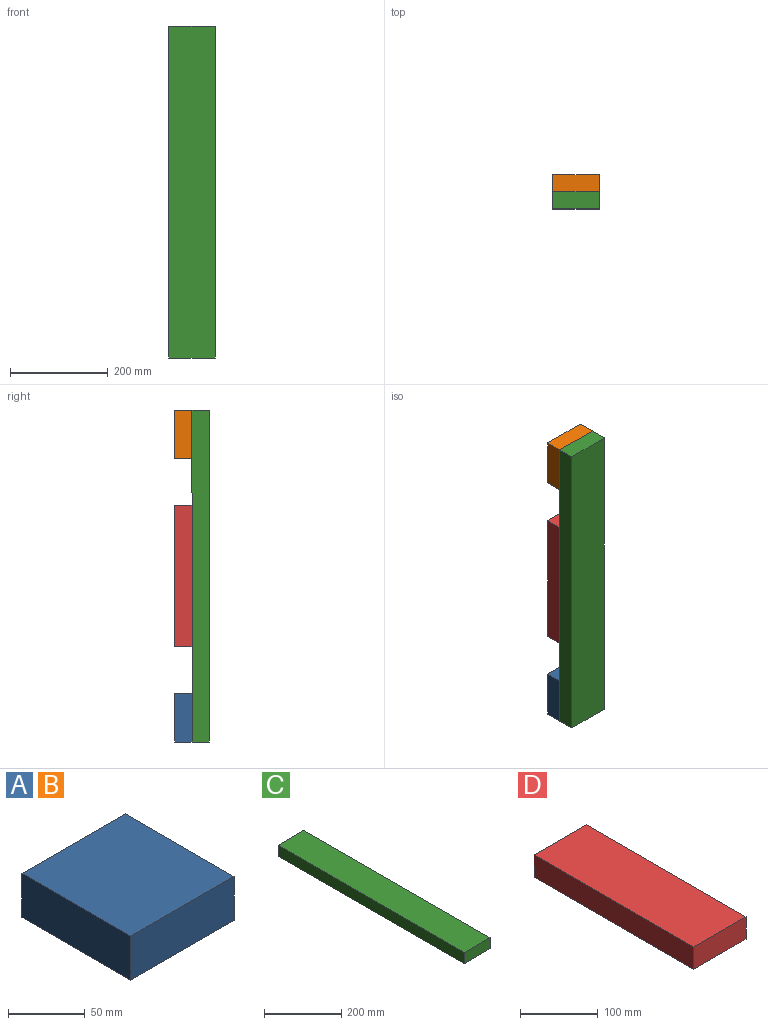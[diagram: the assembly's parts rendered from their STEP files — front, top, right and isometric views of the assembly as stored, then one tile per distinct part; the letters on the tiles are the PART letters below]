
ASSEMBLY  parts=4 mates=3
PART A: 6 faces, bbox 95x100x35 mm
  f0: plane 100x35mm, normal (1,0,0), area 3500mm2, adj f1,f3,f4,f5
  f1: plane 100x95mm, normal (0,0,1), area 9500mm2, adj f0,f2,f4,f5
  f2: plane 100x35mm, normal (-1,0,0), area 3500mm2, adj f1,f3,f4,f5
  f3: plane 100x95mm, normal (0,0,-1), area 9500mm2, adj f0,f2,f4,f5
  f4: plane 95x35mm, normal (0,-1,0), area 3325mm2, adj f0,f1,f2,f3
  f5: plane 95x35mm, normal (0,1,0), area 3325mm2, adj f0,f1,f2,f3
PART B: same geometry as A
PART C: 6 faces, bbox 95x680x35 mm
  f0: plane 680x35mm, normal (1,0,0), area 23800mm2, adj f1,f3,f4,f5
  f1: plane 680x95mm, normal (0,0,1), area 64600mm2, adj f0,f2,f4,f5
  f2: plane 680x35mm, normal (-1,0,0), area 23800mm2, adj f1,f3,f4,f5
  f3: plane 680x95mm, normal (0,0,-1), area 64600mm2, adj f0,f2,f4,f5
  f4: plane 95x35mm, normal (0,-1,0), area 3325mm2, adj f0,f1,f2,f3
  f5: plane 95x35mm, normal (0,1,0), area 3325mm2, adj f0,f1,f2,f3
PART D: 6 faces, bbox 95x290x35 mm
  f0: plane 290x35mm, normal (1,0,0), area 10150mm2, adj f1,f3,f4,f5
  f1: plane 290x95mm, normal (0,0,1), area 27550mm2, adj f0,f2,f4,f5
  f2: plane 290x35mm, normal (-1,0,0), area 10150mm2, adj f1,f3,f4,f5
  f3: plane 290x95mm, normal (0,0,-1), area 27550mm2, adj f0,f2,f4,f5
  f4: plane 95x35mm, normal (0,-1,0), area 3325mm2, adj f0,f1,f2,f3
  f5: plane 95x35mm, normal (0,1,0), area 3325mm2, adj f0,f1,f2,f3
PLACE A rot(axis=(-1,0,0),90deg) t=(0,35,0)mm
PLACE B rot(axis=(-1,0,0),90deg) t=(0,35,580)mm
PLACE C rot(axis=(-1,0,0),90deg) t=(0,0,0)mm fixed
PLACE D rot(axis=(-1,0,0),90deg) t=(0,35,195)mm
MATE fastened D.f3 <-> C.f1  axis (0,-1,0) through (0,17.5,340)mm
MATE fastened B.f3 <-> C.f1  axis (0,-1,0) through (0,17.5,680)mm
MATE fastened A.f3 <-> C.f1  axis (0,-1,0) through (0,17.5,0)mm
